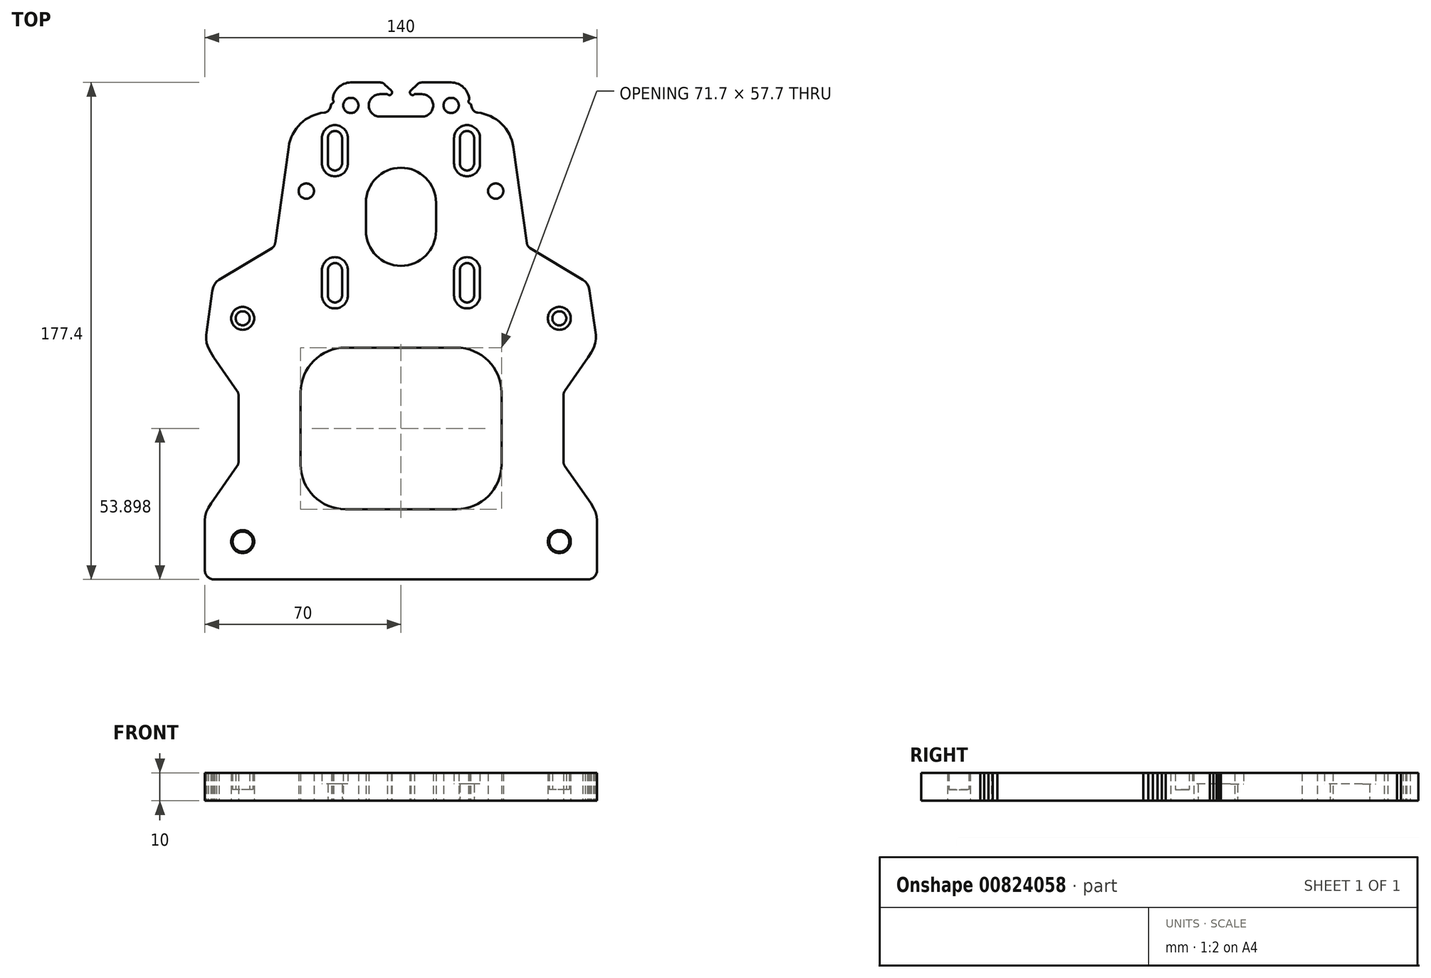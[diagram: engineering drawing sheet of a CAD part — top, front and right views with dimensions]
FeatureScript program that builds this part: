
annotation { "Feature Type Name" : "Feature", "Feature Type Description" : "" }
export const myFeature = defineFeature(function(context is Context, id is Id, definition is map)
    precondition{}
    {
        {
            var Q0;
            Q0=qCreatedBy(makeId("Top.planeOp"),FACE);
            var sketch = newSketch(context, id + "F0", { "sketchPlane" : qUnion([Q0])});
            skLineSegment(sketch, "E0", {"start": v(-66.64, -88.7) * mm, "end": v(66.64, -88.7) * mm});
            skLineSegment(sketch, "E1", {"start": v(-70, -67.59) * mm, "end": v(-70, -85.34) * mm});
            skLineSegment(sketch, "E2", {"start": v(-69.52, -1.4) * mm, "end": v(-67.3, 14.33) * mm});
            skLineSegment(sketch, "E3", {"start": v(-67.3, 14.33) * mm, "end": v(-67, 15.67) * mm});
            skLineSegment(sketch, "E4", {"start": v(-67, 15.67) * mm, "end": v(-66.46, 16.77) * mm});
            skLineSegment(sketch, "E5", {"start": v(-66.46, 16.77) * mm, "end": v(-65.76, 17.64) * mm});
            skLineSegment(sketch, "E6", {"start": v(-65.76, 17.64) * mm, "end": v(-64.88, 18.32) * mm});
            skLineSegment(sketch, "E7", {"start": v(-70, -67.59) * mm, "end": v(-69.87, -66.2) * mm});
            skLineSegment(sketch, "E8", {"start": v(-69.87, -66.2) * mm, "end": v(-69.45, -64.71) * mm});
            skLineSegment(sketch, "E9", {"start": v(-69.45, -64.71) * mm, "end": v(-68.73, -63.15) * mm});
            skLineSegment(sketch, "E10", {"start": v(-68.73, -63.15) * mm, "end": v(-67.73, -61.54) * mm});
            skLineSegment(sketch, "E11", {"start": v(3.5, 85.85) * mm, "end": v(5.82, 88.05) * mm});
            skLineSegment(sketch, "E12", {"start": v(-19.8, -63.65) * mm, "end": v(19.8, -63.65) * mm});
            skLineSegment(sketch, "E13", {"start": v(-58.43, -21.42) * mm, "end": v(-66.79, -9.43) * mm});
            skLineSegment(sketch, "E14", {"start": v(-66.79, -9.43) * mm, "end": v(-67.92, -7.65) * mm});
            skLineSegment(sketch, "E15", {"start": v(-67.92, -7.65) * mm, "end": v(-68.76, -5.94) * mm});
            skLineSegment(sketch, "E16", {"start": v(-68.76, -5.94) * mm, "end": v(-69.32, -4.3) * mm});
            skLineSegment(sketch, "E17", {"start": v(-69.32, -4.3) * mm, "end": v(-69.56, -2.78) * mm});
            skLineSegment(sketch, "E18", {"start": v(-69.56, -2.78) * mm, "end": v(-69.52, -1.4) * mm});
            skLineSegment(sketch, "E19", {"start": v(-58, -46.83) * mm, "end": v(-58, -22.76) * mm});
            skLineSegment(sketch, "E20", {"start": v(-44.92, 31.33) * mm, "end": v(-40.1, 65.65) * mm});
            skLineSegment(sketch, "E21", {"start": v(-25.35, 79.55) * mm, "end": v(-24.83, 81.12) * mm});
            skLineSegment(sketch, "E22", {"start": v(-64.88, 18.32) * mm, "end": v(-46.03, 29.64) * mm});
            skLineSegment(sketch, "E23", {"start": v(-35.85, -22) * mm, "end": v(-35.85, -47.6) * mm});
            skLineSegment(sketch, "E24", {"start": v(-26.11, 68.84) * mm, "end": v(-26.11, 59.84) * mm});
            skLineSegment(sketch, "E25", {"start": v(-26.11, 21.7) * mm, "end": v(-26.11, 12.7) * mm});
            skLineSegment(sketch, "E26", {"start": v(-21.03, 12.7) * mm, "end": v(-21.03, 21.7) * mm});
            skLineSegment(sketch, "E27", {"start": v(-21.03, 59.84) * mm, "end": v(-21.03, 68.84) * mm});
            skLineSegment(sketch, "E28", {"start": v(-67.73, -61.54) * mm, "end": v(-58.43, -48.18) * mm});
            skLineSegment(sketch, "E29", {"start": v(-12.5, 45.77) * mm, "end": v(-12.5, 35.77) * mm});
            skLineSegment(sketch, "E30", {"start": v(19.8, -5.95) * mm, "end": v(-19.8, -5.95) * mm});
            skLineSegment(sketch, "E31", {"start": v(12.5, 35.77) * mm, "end": v(12.5, 45.77) * mm});
            skLineSegment(sketch, "E32", {"start": v(21.03, 68.84) * mm, "end": v(21.03, 59.84) * mm});
            skLineSegment(sketch, "E33", {"start": v(21.03, 21.7) * mm, "end": v(21.03, 12.7) * mm});
            skLineSegment(sketch, "E34", {"start": v(58.43, -48.17) * mm, "end": v(67.73, -61.54) * mm});
            skLineSegment(sketch, "E35", {"start": v(26.11, 12.7) * mm, "end": v(26.11, 21.7) * mm});
            skLineSegment(sketch, "E36", {"start": v(26.11, 59.84) * mm, "end": v(26.11, 68.84) * mm});
            skLineSegment(sketch, "E37", {"start": v(35.85, -47.6) * mm, "end": v(35.85, -22) * mm});
            skLineSegment(sketch, "E38", {"start": v(46.03, 29.64) * mm, "end": v(64.88, 18.32) * mm});
            skLineSegment(sketch, "E39", {"start": v(24.83, 81.12) * mm, "end": v(25.35, 79.55) * mm});
            skLineSegment(sketch, "E40", {"start": v(40.1, 65.65) * mm, "end": v(44.92, 31.33) * mm});
            skLineSegment(sketch, "E41", {"start": v(58, -22.76) * mm, "end": v(58, -46.83) * mm});
            skLineSegment(sketch, "E42", {"start": v(66.78, -9.43) * mm, "end": v(58.43, -21.42) * mm});
            skLineSegment(sketch, "E43", {"start": v(64.88, 18.32) * mm, "end": v(65.78, 17.62) * mm});
            skLineSegment(sketch, "E44", {"start": v(65.78, 17.62) * mm, "end": v(66.49, 16.74) * mm});
            skLineSegment(sketch, "E45", {"start": v(66.49, 16.74) * mm, "end": v(67, 15.65) * mm});
            skLineSegment(sketch, "E46", {"start": v(67, 15.65) * mm, "end": v(67.3, 14.33) * mm});
            skLineSegment(sketch, "E47", {"start": v(-5.82, 88.05) * mm, "end": v(-3.5, 85.85) * mm});
            skLineSegment(sketch, "E48", {"start": v(70, -67.59) * mm, "end": v(69.87, -66.2) * mm});
            skLineSegment(sketch, "E49", {"start": v(69.87, -66.2) * mm, "end": v(69.45, -64.71) * mm});
            skLineSegment(sketch, "E50", {"start": v(69.45, -64.71) * mm, "end": v(68.73, -63.15) * mm});
            skLineSegment(sketch, "E51", {"start": v(68.73, -63.15) * mm, "end": v(67.73, -61.54) * mm});
            skLineSegment(sketch, "E52", {"start": v(67.3, 14.33) * mm, "end": v(69.52, -1.4) * mm});
            skLineSegment(sketch, "E53", {"start": v(69.52, -1.4) * mm, "end": v(69.57, -2.78) * mm});
            skLineSegment(sketch, "E54", {"start": v(69.57, -2.78) * mm, "end": v(69.32, -4.3) * mm});
            skLineSegment(sketch, "E55", {"start": v(69.32, -4.3) * mm, "end": v(68.76, -5.94) * mm});
            skLineSegment(sketch, "E56", {"start": v(68.76, -5.94) * mm, "end": v(67.91, -7.65) * mm});
            skLineSegment(sketch, "E57", {"start": v(67.91, -7.65) * mm, "end": v(66.78, -9.43) * mm});
            skLineSegment(sketch, "E58", {"start": v(70, -85.34) * mm, "end": v(70, -67.59) * mm});
            skLineSegment(sketch, "E59", {"start": v(-7.5, 76.5) * mm, "end": v(7.5, 76.5) * mm});
            skLineSegment(sketch, "E60", {"start": v(7.5, 84.5) * mm, "end": v(4.85, 84.5) * mm});
            skLineSegment(sketch, "E61", {"start": v(-4.85, 84.5) * mm, "end": v(-7.5, 84.5) * mm});
            skLineSegment(sketch, "E62", {"start": v(17.91, 88.7) * mm, "end": v(7.44, 88.7) * mm});
            skLineSegment(sketch, "E63", {"start": v(-7.44, 88.7) * mm, "end": v(-17.91, 88.7) * mm});
            skArc(sketch, "E64", {"start": v(-19.8, -5.95) * mm, "mid": v(-31.15, -10.65) * mm, "end": v(-35.85, -22) * mm});
            skArc(sketch, "E65", {"start": v(-35.85, -47.6) * mm, "mid": v(-31.15, -58.95) * mm, "end": v(-19.8, -63.65) * mm});
            skCircle(sketch, "E66", {"center": v(-56.5, -75.18) * mm, "radius": 3.6 * mm});
            skArc(sketch, "E67", {"start": v(-70, -85.34) * mm, "mid": v(-69.02, -87.72) * mm, "end": v(-66.64, -88.7) * mm});
            skArc(sketch, "E68", {"start": v(-58, -22.76) * mm, "mid": v(-58.11, -22.06) * mm, "end": v(-58.43, -21.42) * mm});
            skArc(sketch, "E69", {"start": v(-58.43, -48.18) * mm, "mid": v(-58.11, -47.54) * mm, "end": v(-58, -46.83) * mm});
            skArc(sketch, "E70", {"start": v(-27.34, 77.95) * mm, "mid": v(-35.84, 74) * mm, "end": v(-40.1, 65.65) * mm});
            skArc(sketch, "E71", {"start": v(-17.91, 88.7) * mm, "mid": v(-22.37, 86.91) * mm, "end": v(-24.36, 82.54) * mm});
            skArc(sketch, "E72", {"start": v(-7.5, 84.5) * mm, "mid": v(-11.5, 80.5) * mm, "end": v(-7.5, 76.5) * mm});
            skCircle(sketch, "E73", {"center": v(-17.9, 80.5) * mm, "radius": 2.73 * mm});
            skCircle(sketch, "E74", {"center": v(-33.8, 49.95) * mm, "radius": 2.73 * mm});
            skArc(sketch, "E75", {"start": v(-21.03, 68.84) * mm, "mid": v(-23.57, 71.38) * mm, "end": v(-26.1, 68.84) * mm});
            skArc(sketch, "E76", {"start": v(-26.1, 59.84) * mm, "mid": v(-23.57, 57.3) * mm, "end": v(-21.03, 59.84) * mm});
            skArc(sketch, "E77", {"start": v(-21.03, 21.7) * mm, "mid": v(-23.57, 24.24) * mm, "end": v(-26.1, 21.7) * mm});
            skArc(sketch, "E78", {"start": v(-26.1, 12.7) * mm, "mid": v(-23.57, 10.16) * mm, "end": v(-21.03, 12.7) * mm});
            skCircle(sketch, "E79", {"center": v(-56.5, 4.52) * mm, "radius": 2.5 * mm});
            skArc(sketch, "E80", {"start": v(-46.03, 29.64) * mm, "mid": v(-45.29, 30.36) * mm, "end": v(-44.92, 31.33) * mm});
            skArc(sketch, "E81", {"start": v(-27.34, 77.95) * mm, "mid": v(-26.1, 78.46) * mm, "end": v(-25.35, 79.55) * mm});
            skArc(sketch, "E82", {"start": v(-5.82, 88.05) * mm, "mid": v(-6.57, 88.53) * mm, "end": v(-7.44, 88.7) * mm});
            skArc(sketch, "E83", {"start": v(-4.85, 84.5) * mm, "mid": v(-3.47, 84.47) * mm, "end": v(-3.5, 85.85) * mm});
            skArc(sketch, "E84", {"start": v(-24.83, 81.12) * mm, "mid": v(-24.12, 81.67) * mm, "end": v(-24.36, 82.54) * mm});
            skArc(sketch, "E85", {"start": v(19.8, -63.65) * mm, "mid": v(31.15, -58.95) * mm, "end": v(35.85, -47.6) * mm});
            skArc(sketch, "E86", {"start": v(35.85, -22) * mm, "mid": v(31.15, -10.65) * mm, "end": v(19.8, -5.95) * mm});
            skCircle(sketch, "E87", {"center": v(56.5, -75.18) * mm, "radius": 3.6 * mm});
            skArc(sketch, "E88", {"start": v(66.64, -88.7) * mm, "mid": v(69.02, -87.72) * mm, "end": v(70, -85.34) * mm});
            skArc(sketch, "E89", {"start": v(58.43, -21.42) * mm, "mid": v(58.12, -22.06) * mm, "end": v(58.01, -22.76) * mm});
            skArc(sketch, "E90", {"start": v(58.01, -46.83) * mm, "mid": v(58.12, -47.54) * mm, "end": v(58.43, -48.17) * mm});
            skArc(sketch, "E91", {"start": v(40.1, 65.65) * mm, "mid": v(35.84, 74) * mm, "end": v(27.34, 77.95) * mm});
            skArc(sketch, "E92", {"start": v(12.5, 45.77) * mm, "mid": v(0, 58.27) * mm, "end": v(-12.5, 45.77) * mm});
            skArc(sketch, "E93", {"start": v(-12.5, 35.77) * mm, "mid": v(0, 23.27) * mm, "end": v(12.5, 35.77) * mm});
            skArc(sketch, "E94", {"start": v(24.36, 82.54) * mm, "mid": v(22.37, 86.91) * mm, "end": v(17.91, 88.7) * mm});
            skArc(sketch, "E95", {"start": v(7.5, 76.5) * mm, "mid": v(11.5, 80.5) * mm, "end": v(7.5, 84.5) * mm});
            skCircle(sketch, "E96", {"center": v(17.9, 80.5) * mm, "radius": 2.73 * mm});
            skCircle(sketch, "E97", {"center": v(33.8, 49.95) * mm, "radius": 2.73 * mm});
            skArc(sketch, "E98", {"start": v(26.1, 68.84) * mm, "mid": v(23.57, 71.38) * mm, "end": v(21.03, 68.84) * mm});
            skArc(sketch, "E99", {"start": v(21.03, 59.84) * mm, "mid": v(23.57, 57.3) * mm, "end": v(26.1, 59.84) * mm});
            skArc(sketch, "E100", {"start": v(26.1, 21.7) * mm, "mid": v(23.57, 24.24) * mm, "end": v(21.03, 21.7) * mm});
            skArc(sketch, "E101", {"start": v(21.03, 12.7) * mm, "mid": v(23.57, 10.16) * mm, "end": v(26.1, 12.7) * mm});
            skCircle(sketch, "E102", {"center": v(56.5, 4.52) * mm, "radius": 2.5 * mm});
            skArc(sketch, "E103", {"start": v(44.92, 31.33) * mm, "mid": v(45.29, 30.36) * mm, "end": v(46.03, 29.64) * mm});
            skArc(sketch, "E104", {"start": v(25.35, 79.55) * mm, "mid": v(26.1, 78.46) * mm, "end": v(27.34, 77.95) * mm});
            skArc(sketch, "E105", {"start": v(7.44, 88.7) * mm, "mid": v(6.57, 88.53) * mm, "end": v(5.82, 88.05) * mm});
            skArc(sketch, "E106", {"start": v(3.5, 85.85) * mm, "mid": v(3.47, 84.47) * mm, "end": v(4.85, 84.5) * mm});
            skArc(sketch, "E107", {"start": v(24.36, 82.54) * mm, "mid": v(24.12, 81.67) * mm, "end": v(24.83, 81.12) * mm});
            skLineSegment(sketch, "E108.0", {"start": v(-28.21, 68.84) * mm, "end": v(-28.21, 59.84) * mm});
            skArc(sketch, "E108.1", {"start": v(-18.93, 68.84) * mm, "mid": v(-23.57, 73.48) * mm, "end": v(-28.2, 68.84) * mm});
            skLineSegment(sketch, "E108.2", {"start": v(-18.93, 59.84) * mm, "end": v(-18.93, 68.84) * mm});
            skArc(sketch, "E108.3", {"start": v(-28.2, 59.84) * mm, "mid": v(-23.57, 55.2) * mm, "end": v(-18.93, 59.84) * mm});
            skLineSegment(sketch, "E109.0", {"start": v(18.93, 68.84) * mm, "end": v(18.93, 59.84) * mm});
            skArc(sketch, "E109.1", {"start": v(28.2, 68.84) * mm, "mid": v(23.57, 73.48) * mm, "end": v(18.93, 68.84) * mm});
            skLineSegment(sketch, "E109.2", {"start": v(28.21, 59.84) * mm, "end": v(28.21, 68.84) * mm});
            skArc(sketch, "E109.3", {"start": v(18.93, 59.84) * mm, "mid": v(23.57, 55.2) * mm, "end": v(28.2, 59.84) * mm});
            skLineSegment(sketch, "E110.0", {"start": v(-28.21, 21.7) * mm, "end": v(-28.21, 12.7) * mm});
            skArc(sketch, "E110.1", {"start": v(-18.93, 21.7) * mm, "mid": v(-23.57, 26.34) * mm, "end": v(-28.2, 21.7) * mm});
            skLineSegment(sketch, "E110.2", {"start": v(-18.93, 12.7) * mm, "end": v(-18.93, 21.7) * mm});
            skArc(sketch, "E110.3", {"start": v(-28.2, 12.7) * mm, "mid": v(-23.57, 8.06) * mm, "end": v(-18.93, 12.7) * mm});
            skLineSegment(sketch, "E111.0", {"start": v(18.93, 21.7) * mm, "end": v(18.93, 12.7) * mm});
            skArc(sketch, "E111.1", {"start": v(28.2, 21.7) * mm, "mid": v(23.57, 26.34) * mm, "end": v(18.93, 21.7) * mm});
            skLineSegment(sketch, "E111.2", {"start": v(28.21, 12.7) * mm, "end": v(28.21, 21.7) * mm});
            skArc(sketch, "E111.3", {"start": v(18.93, 12.7) * mm, "mid": v(23.57, 8.06) * mm, "end": v(28.2, 12.7) * mm});
            skCircle(sketch, "E112.0", {"center": v(-56.5, 4.52) * mm, "radius": 4.1 * mm});
            skCircle(sketch, "E113.0", {"center": v(56.5, 4.52) * mm, "radius": 4.1 * mm});
            skCircle(sketch, "E114.0", {"center": v(-56.5, -75.18) * mm, "radius": 4.1 * mm});
            skCircle(sketch, "E115.0", {"center": v(56.5, -75.18) * mm, "radius": 4.1 * mm});
            skSolve(sketch);
        }
        {
            var Q0;
            Q0 = qSketchRegion(id + "F0", true);
            var Q1;
            Q1=makeQuery(id+"F0.imprint","IMPRINT",FACE,{"disambiguationData":[TD([[makeQuery(id+"F0.imprint","IMPRINT",EDGE,{"derivedFrom":sQuery(id+"F0.wireOp",EDGE,"E79")}),1.0]])]});
            var Q2;
            Q2=makeQuery(id+"F0.imprint","IMPRINT",FACE,{"disambiguationData":[TD([[makeQuery(id+"F0.imprint","IMPRINT",EDGE,{"derivedFrom":sQuery(id+"F0.wireOp",EDGE,"E102")}),1.0]])]});
            var Q3;
            Q3=makeQuery(id+"F0.imprint","IMPRINT",FACE,{"disambiguationData":[TD([[makeQuery(id+"F0.imprint","IMPRINT",EDGE,{"derivedFrom":sQuery(id+"F0.wireOp",EDGE,"E87")}),1.0]])]});
            var Q4;
            Q4=makeQuery(id+"F0.imprint","IMPRINT",FACE,{"disambiguationData":[TD([[makeQuery(id+"F0.imprint","IMPRINT",EDGE,{"derivedFrom":sQuery(id+"F0.wireOp",EDGE,"E66")}),1.0]])]});
            extrude(context, id + "F1", {"entities" : qUnion([Q0, Q1, Q2, Q3, Q4]), "depth" : 10 * mm, "offsetDistance" : 25 * mm});
        }
        {
            var Q0;
            Q0=makeQuery(id+"F0.imprint","IMPRINT",FACE,{"disambiguationData":[TD([[makeQuery(id+"F0.imprint","IMPRINT",EDGE,{"derivedFrom":sQuery(id+"F0.wireOp",EDGE,"E25")}),-1.0]])]});
            var Q1;
            Q1=makeQuery(id+"F0.imprint","IMPRINT",FACE,{"disambiguationData":[TD([[makeQuery(id+"F0.imprint","IMPRINT",EDGE,{"derivedFrom":sQuery(id+"F0.wireOp",EDGE,"E24")}),-1.0]])]});
            var Q2;
            Q2=makeQuery(id+"F0.imprint","IMPRINT",FACE,{"disambiguationData":[TD([[makeQuery(id+"F0.imprint","IMPRINT",EDGE,{"derivedFrom":sQuery(id+"F0.wireOp",EDGE,"E32")}),-1.0]])]});
            var Q3;
            Q3=makeQuery(id+"F0.imprint","IMPRINT",FACE,{"disambiguationData":[TD([[makeQuery(id+"F0.imprint","IMPRINT",EDGE,{"derivedFrom":sQuery(id+"F0.wireOp",EDGE,"E33")}),-1.0]])]});
            extrude(context, id + "F2", {"entities" : qUnion([Q0, Q1, Q2, Q3]), "operationType" : NewBodyOperationType.ADD, "depth" : 6 * mm, "offsetDistance" : 25 * mm});
        }
        {
            var Q0;
            Q0=makeQuery(id+"F0.imprint","IMPRINT",FACE,{"disambiguationData":[TD([[makeQuery(id+"F0.imprint","IMPRINT",EDGE,{"derivedFrom":sQuery(id+"F0.wireOp",EDGE,"E66")}),1.0]])]});
            var Q1;
            Q1=makeQuery(id+"F0.imprint","IMPRINT",FACE,{"disambiguationData":[TD([[makeQuery(id+"F0.imprint","IMPRINT",EDGE,{"derivedFrom":sQuery(id+"F0.wireOp",EDGE,"E79")}),1.0]])]});
            var Q2;
            Q2=makeQuery(id+"F0.imprint","IMPRINT",FACE,{"disambiguationData":[TD([[makeQuery(id+"F0.imprint","IMPRINT",EDGE,{"derivedFrom":sQuery(id+"F0.wireOp",EDGE,"E102")}),1.0]])]});
            var Q3;
            Q3=makeQuery(id+"F0.imprint","IMPRINT",FACE,{"disambiguationData":[TD([[makeQuery(id+"F0.imprint","IMPRINT",EDGE,{"derivedFrom":sQuery(id+"F0.wireOp",EDGE,"E87")}),1.0]])]});
            var Q4;
            Q4=makeQuery(id+"F1.opExtrude","CAP_FACE",FACE,{"disambiguationData":[OSD([sQuery(id+"F0.wireOp",EDGE,"E0"),sQuery(id+"F0.wireOp",EDGE,"E1"),sQuery(id+"F0.wireOp",EDGE,"E2"),sQuery(id+"F0.wireOp",EDGE,"E3"),sQuery(id+"F0.wireOp",EDGE,"E4"),sQuery(id+"F0.wireOp",EDGE,"E5"),sQuery(id+"F0.wireOp",EDGE,"E6"),sQuery(id+"F0.wireOp",EDGE,"E7"),sQuery(id+"F0.wireOp",EDGE,"E8"),sQuery(id+"F0.wireOp",EDGE,"E9"),sQuery(id+"F0.wireOp",EDGE,"E10"),sQuery(id+"F0.wireOp",EDGE,"E11"),sQuery(id+"F0.wireOp",EDGE,"E12"),sQuery(id+"F0.wireOp",EDGE,"E13"),sQuery(id+"F0.wireOp",EDGE,"E14"),sQuery(id+"F0.wireOp",EDGE,"E15"),sQuery(id+"F0.wireOp",EDGE,"E16"),sQuery(id+"F0.wireOp",EDGE,"E17"),sQuery(id+"F0.wireOp",EDGE,"E18"),sQuery(id+"F0.wireOp",EDGE,"E19"),sQuery(id+"F0.wireOp",EDGE,"E20"),sQuery(id+"F0.wireOp",EDGE,"E21"),sQuery(id+"F0.wireOp",EDGE,"E22"),sQuery(id+"F0.wireOp",EDGE,"E23"),sQuery(id+"F0.wireOp",EDGE,"E28"),sQuery(id+"F0.wireOp",EDGE,"E29"),sQuery(id+"F0.wireOp",EDGE,"E30"),sQuery(id+"F0.wireOp",EDGE,"E31"),sQuery(id+"F0.wireOp",EDGE,"E34"),sQuery(id+"F0.wireOp",EDGE,"E37"),sQuery(id+"F0.wireOp",EDGE,"E38"),sQuery(id+"F0.wireOp",EDGE,"E39"),sQuery(id+"F0.wireOp",EDGE,"E40"),sQuery(id+"F0.wireOp",EDGE,"E41"),sQuery(id+"F0.wireOp",EDGE,"E42"),sQuery(id+"F0.wireOp",EDGE,"E43"),sQuery(id+"F0.wireOp",EDGE,"E44"),sQuery(id+"F0.wireOp",EDGE,"E45"),sQuery(id+"F0.wireOp",EDGE,"E46"),sQuery(id+"F0.wireOp",EDGE,"E47"),sQuery(id+"F0.wireOp",EDGE,"E48"),sQuery(id+"F0.wireOp",EDGE,"E49"),sQuery(id+"F0.wireOp",EDGE,"E50"),sQuery(id+"F0.wireOp",EDGE,"E51"),sQuery(id+"F0.wireOp",EDGE,"E52"),sQuery(id+"F0.wireOp",EDGE,"E53"),sQuery(id+"F0.wireOp",EDGE,"E54"),sQuery(id+"F0.wireOp",EDGE,"E55"),sQuery(id+"F0.wireOp",EDGE,"E56"),sQuery(id+"F0.wireOp",EDGE,"E57"),sQuery(id+"F0.wireOp",EDGE,"E58"),sQuery(id+"F0.wireOp",EDGE,"E59"),sQuery(id+"F0.wireOp",EDGE,"E60"),sQuery(id+"F0.wireOp",EDGE,"E61"),sQuery(id+"F0.wireOp",EDGE,"E62"),sQuery(id+"F0.wireOp",EDGE,"E63"),sQuery(id+"F0.wireOp",EDGE,"E64"),sQuery(id+"F0.wireOp",EDGE,"E65"),sQuery(id+"F0.wireOp",EDGE,"E66"),sQuery(id+"F0.wireOp",EDGE,"E67"),sQuery(id+"F0.wireOp",EDGE,"E68"),sQuery(id+"F0.wireOp",EDGE,"E69"),sQuery(id+"F0.wireOp",EDGE,"E70"),sQuery(id+"F0.wireOp",EDGE,"E71"),sQuery(id+"F0.wireOp",EDGE,"E72"),sQuery(id+"F0.wireOp",EDGE,"E73"),sQuery(id+"F0.wireOp",EDGE,"E74"),sQuery(id+"F0.wireOp",EDGE,"E79"),sQuery(id+"F0.wireOp",EDGE,"E80"),sQuery(id+"F0.wireOp",EDGE,"E81"),sQuery(id+"F0.wireOp",EDGE,"E82"),sQuery(id+"F0.wireOp",EDGE,"E83"),sQuery(id+"F0.wireOp",EDGE,"E84"),sQuery(id+"F0.wireOp",EDGE,"E85"),sQuery(id+"F0.wireOp",EDGE,"E86"),sQuery(id+"F0.wireOp",EDGE,"E87"),sQuery(id+"F0.wireOp",EDGE,"E88"),sQuery(id+"F0.wireOp",EDGE,"E89"),sQuery(id+"F0.wireOp",EDGE,"E90"),sQuery(id+"F0.wireOp",EDGE,"E91"),sQuery(id+"F0.wireOp",EDGE,"E92"),sQuery(id+"F0.wireOp",EDGE,"E93"),sQuery(id+"F0.wireOp",EDGE,"E94"),sQuery(id+"F0.wireOp",EDGE,"E95"),sQuery(id+"F0.wireOp",EDGE,"E96"),sQuery(id+"F0.wireOp",EDGE,"E97"),sQuery(id+"F0.wireOp",EDGE,"E102"),sQuery(id+"F0.wireOp",EDGE,"E103"),sQuery(id+"F0.wireOp",EDGE,"E104"),sQuery(id+"F0.wireOp",EDGE,"E105"),sQuery(id+"F0.wireOp",EDGE,"E106"),sQuery(id+"F0.wireOp",EDGE,"E107"),sQuery(id+"F0.wireOp",EDGE,"E108.0"),sQuery(id+"F0.wireOp",EDGE,"E108.1"),sQuery(id+"F0.wireOp",EDGE,"E108.2"),sQuery(id+"F0.wireOp",EDGE,"E108.3"),sQuery(id+"F0.wireOp",EDGE,"E109.0"),sQuery(id+"F0.wireOp",EDGE,"E109.1"),sQuery(id+"F0.wireOp",EDGE,"E109.2"),sQuery(id+"F0.wireOp",EDGE,"E109.3"),sQuery(id+"F0.wireOp",EDGE,"E110.0"),sQuery(id+"F0.wireOp",EDGE,"E110.1"),sQuery(id+"F0.wireOp",EDGE,"E110.2"),sQuery(id+"F0.wireOp",EDGE,"E110.3"),sQuery(id+"F0.wireOp",EDGE,"E111.0"),sQuery(id+"F0.wireOp",EDGE,"E111.1"),sQuery(id+"F0.wireOp",EDGE,"E111.2"),sQuery(id+"F0.wireOp",EDGE,"E111.3")])],"isStart":false});
            extrude(context, id + "F3", {"entities" : qUnion([Q0, Q1, Q2, Q3]), "operationType" : NewBodyOperationType.REMOVE, "endBound" : BoundingType.UP_TO_SURFACE, "depth" : 25 * mm, "endBoundEntityFace" : qUnion([Q4]), "hasOffset" : true, "offsetDistance" : 6 * mm});
        }
    });
